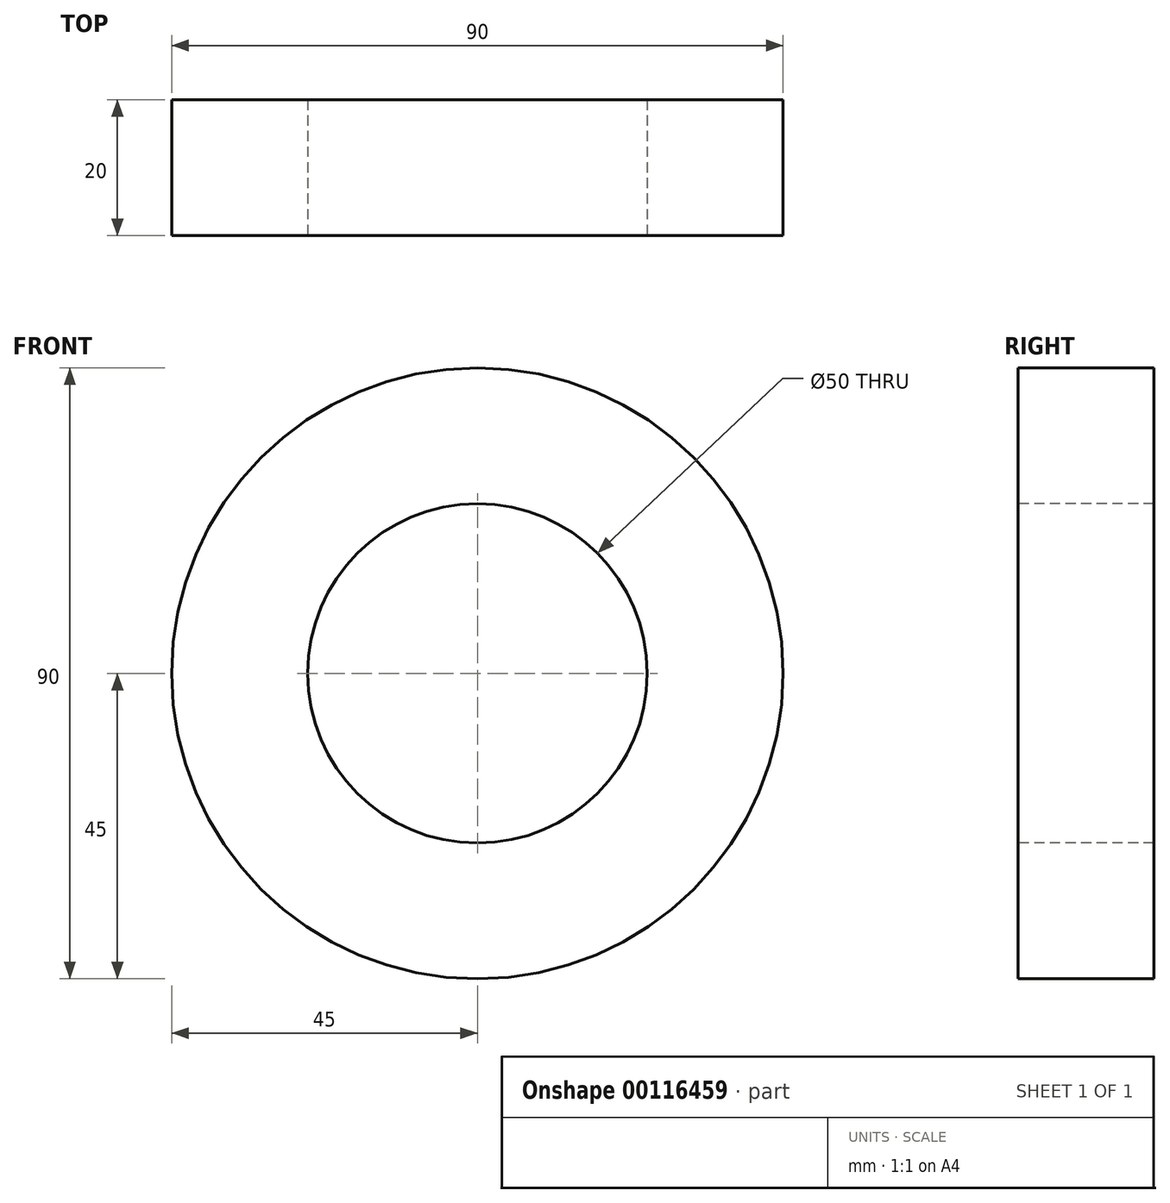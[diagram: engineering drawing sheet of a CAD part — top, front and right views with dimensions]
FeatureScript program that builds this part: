
annotation { "Feature Type Name" : "Feature", "Feature Type Description" : "" }
export const myFeature = defineFeature(function(context is Context, id is Id, definition is map)
    precondition{}
    {
        {
            var Q0;
            Q0=qCreatedBy(makeId("Front.planeOp"),FACE);
            var sketch = newSketch(context, id + "F0", { "sketchPlane" : qUnion([Q0])});
            skCircle(sketch, "E0", {"center": v(0, 0) * mm, "radius": 25 * mm});
            skCircle(sketch, "E1", {"center": v(0, 0) * mm, "radius": 45 * mm});
            skSolve(sketch);
        }
        {
            var Q0;
            Q0=makeQuery(id+"F0.imprint","IMPRINT",FACE,{"disambiguationData":[TD([[makeQuery(id+"F0.imprint","IMPRINT",EDGE,{"derivedFrom":sQuery(id+"F0.wireOp",EDGE,"E0")}),-1.0]])]});
            extrude(context, id + "F1", {"entities" : qUnion([Q0]), "oppositeDirection" : true, "depth" : 20 * mm});
        }
    });
